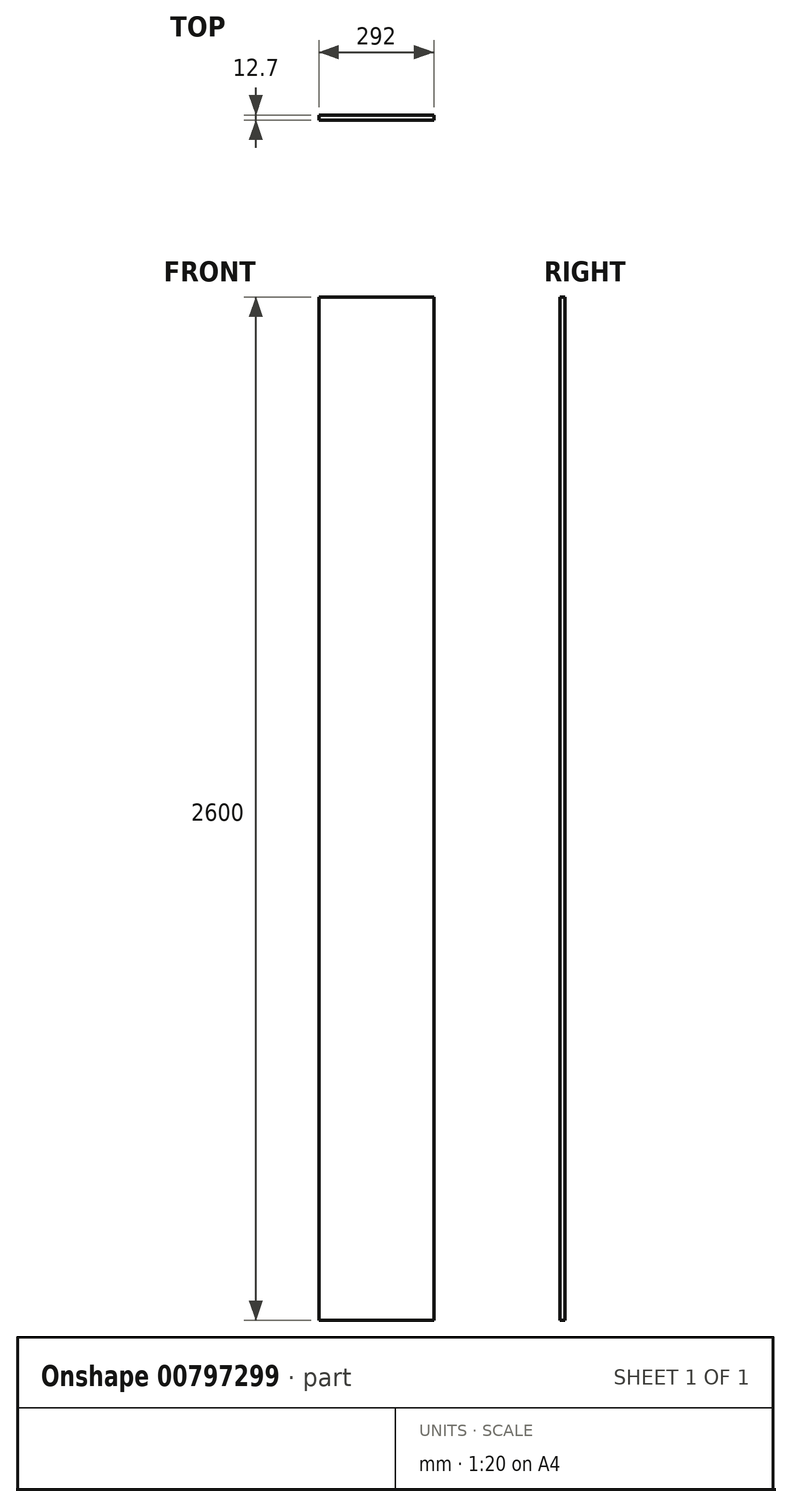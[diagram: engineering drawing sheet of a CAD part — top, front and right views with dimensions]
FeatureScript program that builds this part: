
annotation { "Feature Type Name" : "Feature", "Feature Type Description" : "" }
export const myFeature = defineFeature(function(context is Context, id is Id, definition is map)
    precondition{}
    {
        {
            var Q0;
            Q0=qCreatedBy(makeId("Front.planeOp"),FACE);
            var sketch = newSketch(context, id + "F0", { "sketchPlane" : qUnion([Q0])});
            skLineSegment(sketch, "E0.bottom", {"start": v(146, -1300) * mm, "end": v(-146, -1300) * mm});
            skLineSegment(sketch, "E0.top", {"start": v(146, 1300) * mm, "end": v(-146, 1300) * mm});
            skLineSegment(sketch, "E0.left", {"start": v(146, -1300) * mm, "end": v(146, 1300) * mm});
            skLineSegment(sketch, "E0.right", {"start": v(-146, -1300) * mm, "end": v(-146, 1300) * mm});
            skPoint(sketch, "E0.middle", {"position": v(0, 0) * mm});
            skSolve(sketch);
        }
        {
            var Q0;
            Q0=qSketchRegion(id+"F0",true);
            extrude(context, id + "F1", {"entities" : qUnion([Q0]), "depth" : (25.4 / 2) * mm, "offsetDistance" : 25 * mm, "symmetric" : true});
        }
    });
